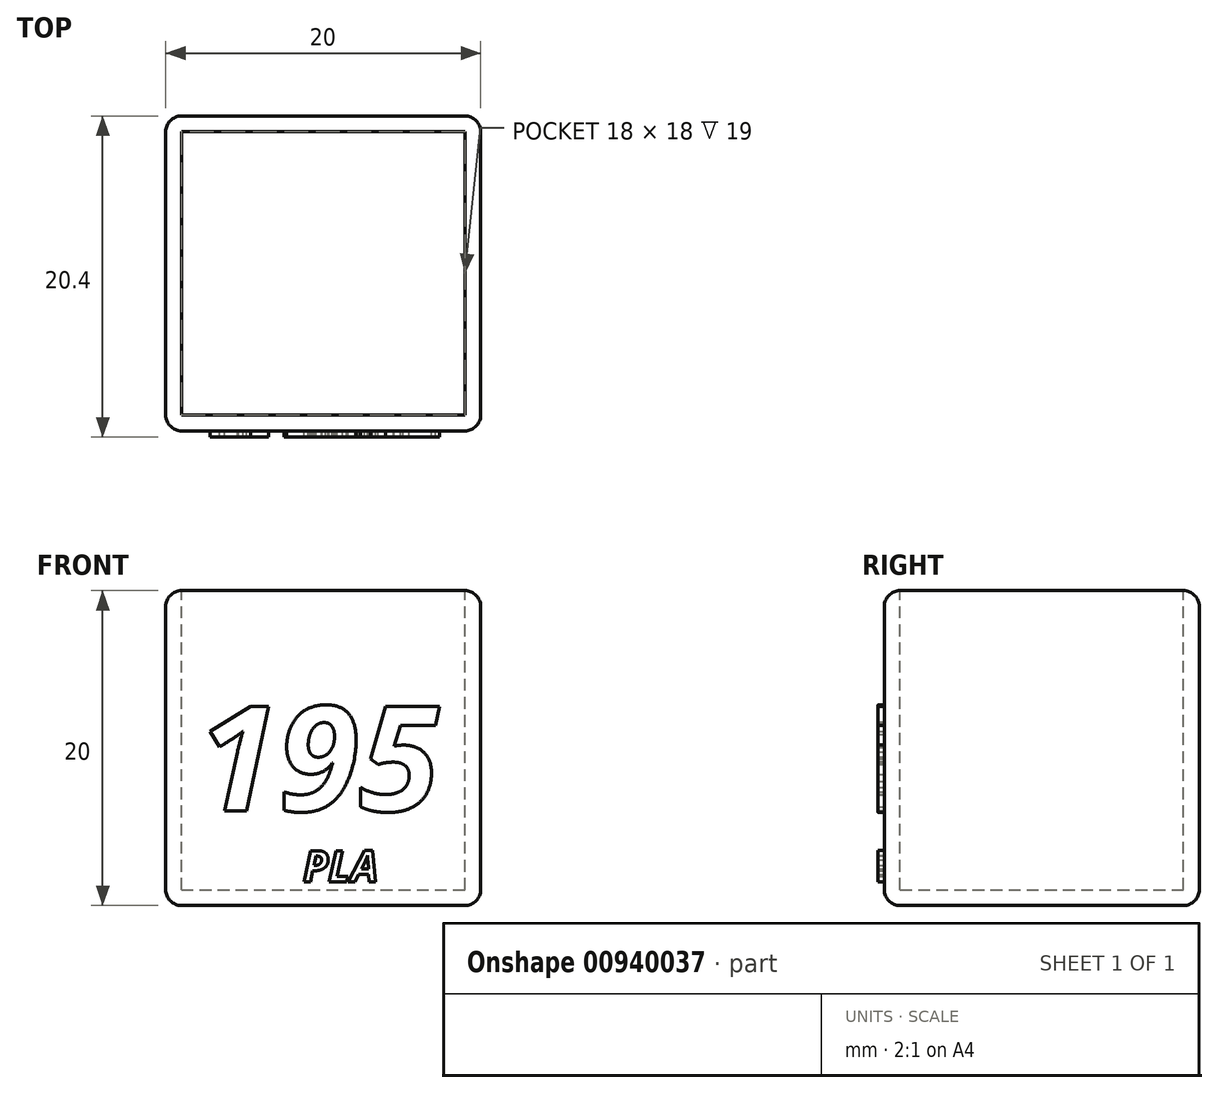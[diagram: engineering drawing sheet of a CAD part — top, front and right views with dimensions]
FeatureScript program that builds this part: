
annotation { "Feature Type Name" : "Feature", "Feature Type Description" : "" }
export const myFeature = defineFeature(function(context is Context, id is Id, definition is map)
    precondition{}
    {
        {
            var Q0;
            Q0=qCreatedBy(makeId("Top.planeOp"),FACE);
            var sketch = newSketch(context, id + "F0", { "sketchPlane" : qUnion([Q0])});
            skLineSegment(sketch, "E0.bottom", {"start": v(10, -10) * mm, "end": v(-10, -10) * mm});
            skLineSegment(sketch, "E0.top", {"start": v(10, 10) * mm, "end": v(-10, 10) * mm});
            skLineSegment(sketch, "E0.left", {"start": v(10, -10) * mm, "end": v(10, 10) * mm});
            skLineSegment(sketch, "E0.right", {"start": v(-10, -10) * mm, "end": v(-10, 10) * mm});
            skPoint(sketch, "E0.middle", {"position": v(0, 0) * mm});
            skSolve(sketch);
        }
        {
            var Q0;
            Q0 = qSketchRegion(id + "F0", true);
            extrude(context, id + "F1", {"entities" : qUnion([Q0]), "depth" : 20 * mm, "offsetDistance" : 25 * mm});
        }
        {
            var Q0;
            Q0=makeQuery(id+"F1.opExtrude","SWEPT_EDGE",EDGE,{"disambiguationData":[OSD([sQuery(id+"F0.wireOp",EDGE,"E0.top"),sQuery(id+"F0.wireOp",EDGE,"E0.left")])]});
            var Q1;
            Q1=makeQuery(id+"F1.opExtrude","SWEPT_EDGE",EDGE,{"disambiguationData":[OSD([sQuery(id+"F0.wireOp",EDGE,"E0.bottom"),sQuery(id+"F0.wireOp",EDGE,"E0.right")])]});
            var Q2;
            Q2=makeQuery(id+"F1.opExtrude","SWEPT_EDGE",EDGE,{"disambiguationData":[OSD([sQuery(id+"F0.wireOp",EDGE,"E0.bottom"),sQuery(id+"F0.wireOp",EDGE,"E0.left")])]});
            var Q3;
            Q3=makeQuery(id+"F1.opExtrude","SWEPT_EDGE",EDGE,{"disambiguationData":[OSD([sQuery(id+"F0.wireOp",EDGE,"E0.top"),sQuery(id+"F0.wireOp",EDGE,"E0.right")])]});
            var Q4;
            Q4=makeQuery(id+"F1.opExtrude","CAP_EDGE",EDGE,{"disambiguationData":[OSD([sQuery(id+"F0.wireOp",EDGE,"E0.left")])],"isStart":true});
            var Q5;
            Q5=makeQuery(id+"F1.opExtrude","CAP_EDGE",EDGE,{"disambiguationData":[OSD([sQuery(id+"F0.wireOp",EDGE,"E0.bottom")])],"isStart":true});
            var Q6;
            Q6=makeQuery(id+"F1.opExtrude","CAP_EDGE",EDGE,{"disambiguationData":[OSD([sQuery(id+"F0.wireOp",EDGE,"E0.top")])],"isStart":true});
            var Q7;
            Q7=makeQuery(id+"F1.opExtrude","CAP_EDGE",EDGE,{"disambiguationData":[OSD([sQuery(id+"F0.wireOp",EDGE,"E0.right")])],"isStart":true});
            fillet(context, id + "F2", {"entities" : qUnion([Q0, Q1, Q2, Q3, Q4, Q5, Q6, Q7]), "radius" : 1 * mm, "tangentPropagation" : true, "allowEdgeOverflow" : false});
        }
        {
            var Q0;
            Q0=makeQuery(id+"F1.opExtrude","CAP_FACE",FACE,{"disambiguationData":[OSD([sQuery(id+"F0.wireOp",EDGE,"E0.bottom"),sQuery(id+"F0.wireOp",EDGE,"E0.top"),sQuery(id+"F0.wireOp",EDGE,"E0.left"),sQuery(id+"F0.wireOp",EDGE,"E0.right")])],"isStart":false});
            shell(context, id + "F3", {"entities" : qUnion([Q0]), "thickness" : 1 * mm});
        }
        {
            var Q0;
            {var subQ0=sQuery(id+"F0.wireOp",EDGE,"E0.left");var subQ1=sQuery(id+"F0.wireOp",EDGE,"E0.top");Q0=makeQuery(id+"F2.opFillet","BLEND_EDGE",EDGE,{"blendedFrom":[makeQuery(id+"F1.opExtrude","SWEPT_EDGE",EDGE,{"disambiguationData":[OSD([subQ1,subQ0])]}),makeQuery(id+"F1.opExtrude","CAP_FACE",FACE,{"disambiguationData":[OSD([sQuery(id+"F0.wireOp",EDGE,"E0.bottom"),subQ1,subQ0,sQuery(id+"F0.wireOp",EDGE,"E0.right")])],"isStart":false})],"blendedInto":[makeQuery(id+"F1.opExtrude","CAP_FACE",FACE,{"disambiguationData":[OSD([sQuery(id+"F0.wireOp",EDGE,"E0.bottom"),subQ1,subQ0,sQuery(id+"F0.wireOp",EDGE,"E0.right")])],"isStart":false})]});}
            var Q1;
            {var subQ0=sQuery(id+"F0.wireOp",EDGE,"E0.right");var subQ1=sQuery(id+"F0.wireOp",EDGE,"E0.top");Q1=makeQuery(id+"F2.opFillet","BLEND_EDGE",EDGE,{"blendedFrom":[makeQuery(id+"F1.opExtrude","SWEPT_EDGE",EDGE,{"disambiguationData":[OSD([subQ1,subQ0])]}),makeQuery(id+"F1.opExtrude","CAP_FACE",FACE,{"disambiguationData":[OSD([sQuery(id+"F0.wireOp",EDGE,"E0.bottom"),subQ1,sQuery(id+"F0.wireOp",EDGE,"E0.left"),subQ0])],"isStart":false})],"blendedInto":[makeQuery(id+"F1.opExtrude","CAP_FACE",FACE,{"disambiguationData":[OSD([sQuery(id+"F0.wireOp",EDGE,"E0.bottom"),subQ1,sQuery(id+"F0.wireOp",EDGE,"E0.left"),subQ0])],"isStart":false})]});}
            var Q2;
            Q2=makeQuery(id+"F1.opExtrude","CAP_EDGE",EDGE,{"disambiguationData":[OSD([sQuery(id+"F0.wireOp",EDGE,"E0.bottom")])],"isStart":false});
            var Q3;
            Q3=makeQuery(id+"F1.opExtrude","CAP_EDGE",EDGE,{"disambiguationData":[OSD([sQuery(id+"F0.wireOp",EDGE,"E0.top")])],"isStart":false});
            var Q4;
            {var subQ0=sQuery(id+"F0.wireOp",EDGE,"E0.right");var subQ1=sQuery(id+"F0.wireOp",EDGE,"E0.bottom");Q4=makeQuery(id+"F2.opFillet","BLEND_EDGE",EDGE,{"blendedFrom":[makeQuery(id+"F1.opExtrude","SWEPT_EDGE",EDGE,{"disambiguationData":[OSD([subQ1,subQ0])]}),makeQuery(id+"F1.opExtrude","CAP_FACE",FACE,{"disambiguationData":[OSD([subQ1,sQuery(id+"F0.wireOp",EDGE,"E0.top"),sQuery(id+"F0.wireOp",EDGE,"E0.left"),subQ0])],"isStart":false})],"blendedInto":[makeQuery(id+"F1.opExtrude","CAP_FACE",FACE,{"disambiguationData":[OSD([subQ1,sQuery(id+"F0.wireOp",EDGE,"E0.top"),sQuery(id+"F0.wireOp",EDGE,"E0.left"),subQ0])],"isStart":false})]});}
            var Q5;
            Q5=makeQuery(id+"F1.opExtrude","CAP_EDGE",EDGE,{"disambiguationData":[OSD([sQuery(id+"F0.wireOp",EDGE,"E0.left")])],"isStart":false});
            var Q6;
            Q6=makeQuery(id+"F1.opExtrude","CAP_EDGE",EDGE,{"disambiguationData":[OSD([sQuery(id+"F0.wireOp",EDGE,"E0.right")])],"isStart":false});
            var Q7;
            {var subQ0=sQuery(id+"F0.wireOp",EDGE,"E0.left");var subQ1=sQuery(id+"F0.wireOp",EDGE,"E0.bottom");Q7=makeQuery(id+"F2.opFillet","BLEND_EDGE",EDGE,{"blendedFrom":[makeQuery(id+"F1.opExtrude","SWEPT_EDGE",EDGE,{"disambiguationData":[OSD([subQ1,subQ0])]}),makeQuery(id+"F1.opExtrude","CAP_FACE",FACE,{"disambiguationData":[OSD([subQ1,sQuery(id+"F0.wireOp",EDGE,"E0.top"),subQ0,sQuery(id+"F0.wireOp",EDGE,"E0.right")])],"isStart":false})],"blendedInto":[makeQuery(id+"F1.opExtrude","CAP_FACE",FACE,{"disambiguationData":[OSD([subQ1,sQuery(id+"F0.wireOp",EDGE,"E0.top"),subQ0,sQuery(id+"F0.wireOp",EDGE,"E0.right")])],"isStart":false})]});}
            fillet(context, id + "F4", {"entities" : qUnion([Q0, Q1, Q2, Q3, Q4, Q5, Q6, Q7]), "radius" : 1 * mm, "tangentPropagation" : true, "allowEdgeOverflow" : false});
        }
        {
            var Q0;
            Q0=makeQuery(id+"F1.opExtrude","SWEPT_FACE",FACE,{"disambiguationData":[OSD([sQuery(id+"F0.wireOp",EDGE,"E0.right")])]});
            var sketch = newSketch(context, id + "F5", { "sketchPlane" : qUnion([Q0])});
            skLineSegment(sketch, "E1", {"start": v(-9, 10) * mm, "end": v(0, 19) * mm});
            skLineSegment(sketch, "E2", {"start": v(0, 19) * mm, "end": v(9, 10) * mm});
            skLineSegment(sketch, "E3", {"start": v(9, 10) * mm, "end": v(0, 1) * mm});
            skLineSegment(sketch, "E4", {"start": v(0, 1) * mm, "end": v(-9, 10) * mm});
            skSolve(sketch);
        }
        {
            var Q0;
            Q0=makeQuery(id+"F1.opExtrude","SWEPT_FACE",FACE,{"disambiguationData":[OSD([sQuery(id+"F0.wireOp",EDGE,"E0.top")])]});
            var sketch = newSketch(context, id + "F6", { "sketchPlane" : qUnion([Q0])});
            skLineSegment(sketch, "E5", {"start": v(-9, 10) * mm, "end": v(0, 19) * mm});
            skLineSegment(sketch, "E6", {"start": v(0, 19) * mm, "end": v(9, 10) * mm});
            skLineSegment(sketch, "E7", {"start": v(9, 10) * mm, "end": v(0, 1) * mm});
            skLineSegment(sketch, "E8", {"start": v(0, 1) * mm, "end": v(-9, 10) * mm});
            skSolve(sketch);
        }
        {
            var Q0;
            Q0=makeQuery(id+"F1.opExtrude","SWEPT_FACE",FACE,{"disambiguationData":[OSD([sQuery(id+"F0.wireOp",EDGE,"E0.bottom")])]});
            var sketch = newSketch(context, id + "F7", { "sketchPlane" : qUnion([Q0])});
            skText(sketch, "E9", { "text": "195", "fontName": "OpenSans-BoldItalic.ttf"});
            const initialGuessF7  = {"E9": [-0.008, 0.006, 1, 0, 0.0067]};
            skSetInitialGuess(sketch, initialGuessF7);
            skSolve(sketch);
        }
        {
            var Q0;
            Q0 = qSketchRegion(id + "F7", true);
            extrude(context, id + "F8", {"entities" : qUnion([Q0]), "operationType" : NewBodyOperationType.ADD, "depth" : 0.4 * mm, "offsetDistance" : 25 * mm});
        }
        {
            var Q0;
            {var subQ0=sQuery(id+"F0.wireOp",EDGE,"E0.bottom");Q0=makeQuery(id+"F8.boolean.opBoolean","SPLIT",FACE,{"disambiguationData":[TD([makeQuery(id+"F2.opFillet","BLEND_FACE",FACE,{"disambiguationData":[OSD([subQ0])]})])],"derivedFrom":makeQuery(id+"F1.opExtrude","SWEPT_FACE",FACE,{"disambiguationData":[OSD([subQ0])]})});}
            var sketch = newSketch(context, id + "F9", { "sketchPlane" : qUnion([Q0])});
            skText(sketch, "E10", { "text": "PLA", "fontName": "OpenSans-BoldItalic.ttf"});
            const initialGuessF9  = {"E10": [-0.0013, 0.0015, 1, 0, 0.002]};
            skSetInitialGuess(sketch, initialGuessF9);
            skSolve(sketch);
        }
        {
            var Q0;
            Q0 = qSketchRegion(id + "F9", true);
            extrude(context, id + "F10", {"entities" : qUnion([Q0]), "operationType" : NewBodyOperationType.ADD, "depth" : 0.4 * mm, "offsetDistance" : 25 * mm});
        }
    });
